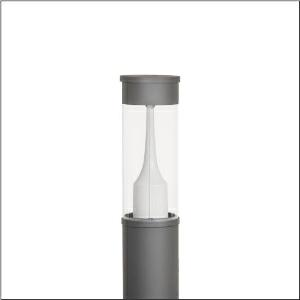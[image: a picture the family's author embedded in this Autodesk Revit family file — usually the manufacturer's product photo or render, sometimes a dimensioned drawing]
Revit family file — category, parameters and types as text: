
# Revit family: city-light_120_iq___p1_0a_5xa5285lf14h_baf3
name_source: partatom
category: Lighting Fixtures
units: mm (PartAtom-declared; Revit-internal decimal feet)

## family parameters
Cut with Voids When Loaded = No
Host = Face
Light Source = No
Part Type = Normal
Room Calculation Point = No
Round Connector Dimension = Use Diameter
Shared = No

## types (1)
- --- (1 x LED, 1510 lm, 10 W, 4000K)
    Apparent Load = 10 VA
    CIE Flux Codes = 32 61 90 93 100
    Color Rendering = 70
    Color Temperature = 4000K
    Default Elevation = 1800 mm
    Description = City-Light 120 iQ, bollard luminaire, Module 540 iQ-SR, primary light control with 3 zone facetted reflector, of plastic, silver coated, highly specular, structured, primary optical cover: cover, of PMMA, transparent, partly coated, light distribution: P1.0a, primary light characteristic: strongly asymmetric, LED, High Power LED, rated luminous flux: 1.510lm, luminous efficacy: 151lm/W, light colour: 740, colour temperature: 4000K, control gear: iQ Street-Remote, control: pre-setting: logarithmic dimming characteristic, Street-Remote, Auto-Match, Temp-Guard, Lumen-Switch, Night-Set, Smart-Wire, Light-Fading, Desk-Remote (wireless, voltage-free reading and setting of iQ features in the workshop via application-optimized NFC function/RFID function), optimised constant luminous flux control (CLO 2.0), with terminal, 6-pole, max. 2.5mm², mains connection: 230..240V, AC, 50/60Hz, start of lifetime: 10W, end of service life: 10W, reduction: 5W, luminaire housing, cylindrical, of extruded aluminium section, coated, Siteco® metallic grey (DB 702S), length: 1.200mm, diameter: 200mm, Module 540 iQ-SR, traffic white (RAL 9016), equipment: standard, protection rating (complete): IP54, insulation class (complete): insulation class II (safety insulation), certification: CE, ENEC, VDE, packaging unit: 1 piece

Light Distribution: P1.0a
    Height = 500 mm
    Lamp = 1 x LED
    Lamp Light Flux = 1510 lm
    Lamp Power = 10 W
    Lamp count = 1
    Length = 200 mm  [stored 0.656168 ft]
    Luminous efficacy = 151 lm/W
    Manufacturer = Siteco
    ModVariant = No
    Model = 5XA5285LF14H
    Mounting Place = Floor
    Mounting Type = Freestanding
    Number of Poles = 1
    OnlyDefault = Yes
    Power Factor = 1
    Product Name = City-Light 120 iQ | P1.0a
    Product group = bollard luminaire
    ProductGroupID = 1304
    Protection Class = Protection class II
    Protection Degree = IP 54
    RLX_Detail_Level = 1
    RLX_Emergency_Light_Flux = 0 lm
    RLX_Emergency_Type = 0
    RLX_Emergency_Type_DB = No
    RlxData = <blob elided: 52197 chars, md5=e9ba7eff>
    Socket = socket
    Standby Power = 0 W
    System Light Flux = 1510 lm
    System Power = 10 W
    Type Comments = factory setting: luminous flux: 100 % | dim-lin: 254 | 401 mA
    Type Image = l_1006922.jpg
    URL = http://relux.com
    VarID = @adj_160597
    Voltage = 0 V
    Weight = 0.00 kg
    Width = 0 mm  [stored 0 ft]

note: [stored X ft] marks values corroborated as IEEE doubles in the binary element streams (Revit-internal decimal feet)

## geometry (parser evidence)
native form markers: Blend x4, Sweep x9
no freeform markers — native parametric forms only
